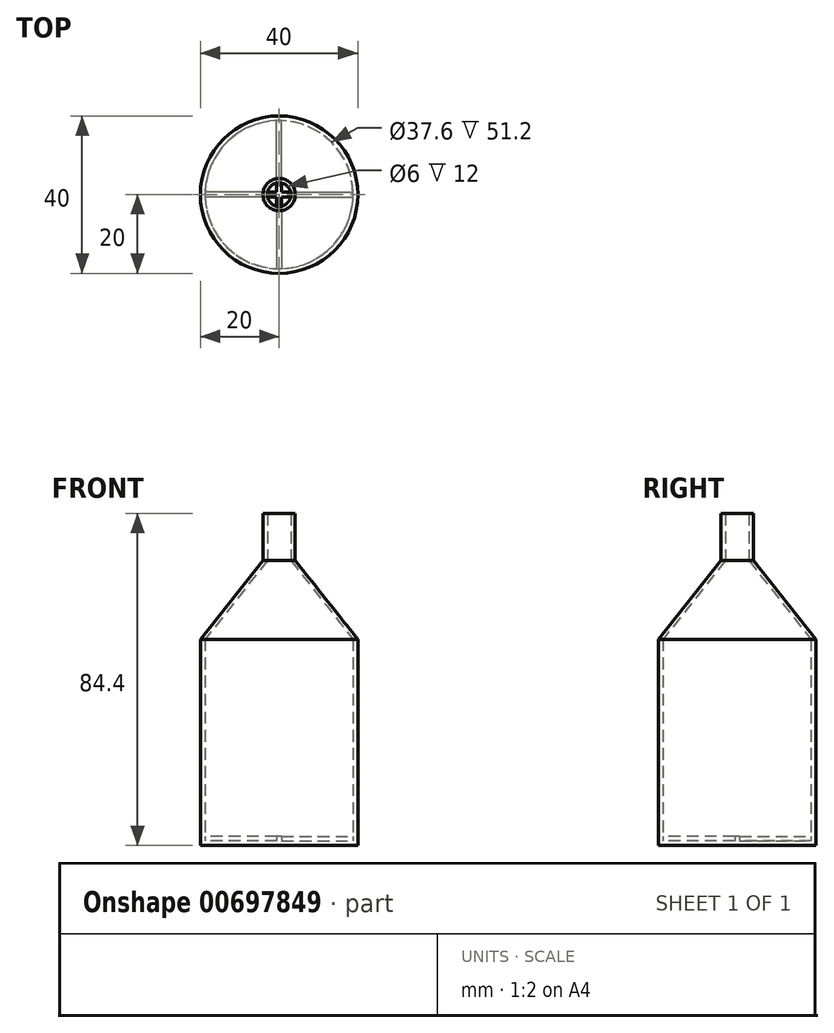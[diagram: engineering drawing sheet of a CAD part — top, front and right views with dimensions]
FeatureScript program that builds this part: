
annotation { "Feature Type Name" : "Feature", "Feature Type Description" : "" }
export const myFeature = defineFeature(function(context is Context, id is Id, definition is map)
    precondition{}
    {
        {
            assignVariable(context, id + "F0", {"name" : "Width", "anyValue" : 0.6});
        }
        {
            var Q0;
            Q0=qCreatedBy(makeId("Top.planeOp"),FACE);
            var sketch = newSketch(context, id + "F1", { "sketchPlane" : qUnion([Q0])});
            skCircle(sketch, "E0", {"center": v(0, 0) * mm, "radius": 20 * mm});
            skLineSegment(sketch, "E1", {"start": v(0, 0) * mm, "end": v(20, 0) * mm, "construction": true});
            skLineSegment(sketch, "E2", {"start": v(0, 0) * mm, "end": v(-20, 0) * mm, "construction": true});
            skLineSegment(sketch, "E3", {"start": v(0, 0) * mm, "end": v(0, 20) * mm, "construction": true});
            skLineSegment(sketch, "E4", {"start": v(0, 0) * mm, "end": v(0, -20) * mm, "construction": true});
            skLineSegment(sketch, "E5.0", {"start": v(0.6, 0.6) * mm, "end": v(0.6, 18.8) * mm});
            skLineSegment(sketch, "E6.0", {"start": v(-0.6, 0.6) * mm, "end": v(-0.6, 18.8) * mm});
            skLineSegment(sketch, "E7.0", {"start": v(-0.6, 0.6) * mm, "end": v(-18.8, 0.6) * mm});
            skLineSegment(sketch, "E8.0", {"start": v(-0.6, -0.6) * mm, "end": v(-18.8, -0.6) * mm});
            skLineSegment(sketch, "E9.0", {"start": v(0.6, -0.6) * mm, "end": v(18.8, -0.6) * mm});
            skLineSegment(sketch, "E10.0", {"start": v(0.6, 0.6) * mm, "end": v(18.8, 0.6) * mm});
            skLineSegment(sketch, "E11.0", {"start": v(-0.6, -0.6) * mm, "end": v(-0.6, -18.8) * mm});
            skLineSegment(sketch, "E12.0", {"start": v(0.6, -0.6) * mm, "end": v(0.6, -18.8) * mm});
            skArc(sketch, "E13.0", {"start": v(-18.8, -0.6) * mm, "mid": v(-13.3, -13.3) * mm, "end": v(-0.6, -18.8) * mm});
            skArc(sketch, "E14.trimOffspring", {"start": v(18.8, 0.6) * mm, "mid": v(13.3, 13.3) * mm, "end": v(0.6, 18.8) * mm});
            skArc(sketch, "E15.trimOffspring", {"start": v(0.6, -18.8) * mm, "mid": v(13.3, -13.3) * mm, "end": v(18.8, -0.6) * mm});
            skArc(sketch, "E16.trimOffspring", {"start": v(-0.6, 18.8) * mm, "mid": v(-13.3, 13.3) * mm, "end": v(-18.8, 0.6) * mm});
            skSolve(sketch);
        }
        {
            var Q0;
            Q0=makeQuery(id+"F1.imprint","IMPRINT",FACE,{"disambiguationData":[TD([[makeQuery(id+"F1.imprint","IMPRINT",EDGE,{"derivedFrom":sQuery(id+"F1.wireOp",EDGE,"E0")}),1.0]])]});
            extrude(context, id + "F2", {"entities" : qUnion([Q0]), "depth" : (getVariable(context, 'Width') * 2) * mm, "offsetDistance" : 25 * mm});
        }
        {
            var Q0;
            Q0=qCreatedBy(makeId("Top.planeOp"),FACE);
            var sketch = newSketch(context, id + "F3", { "sketchPlane" : qUnion([Q0])});
            skCircle(sketch, "E17.0", {"center": v(0, 0) * mm, "radius": 20 * mm});
            skSolve(sketch);
        }
        {
            var Q0;
            Q0=makeQuery(id+"F3.imprint","IMPRINT",FACE,{"disambiguationData":[TD([[makeQuery(id+"F3.imprint","IMPRINT",EDGE,{"derivedFrom":sQuery(id+"F3.wireOp",EDGE,"E17.0")}),1.0]])]});
            extrude(context, id + "F4", {"entities" : qUnion([Q0]), "operationType" : NewBodyOperationType.ADD, "oppositeDirection" : true, "depth" : (getVariable(context, 'Width') * 2) * mm, "offsetDistance" : 25 * mm});
        }
        {
            var Q0;
            Q0=makeQuery(id+"F2.opExtrude","CAP_FACE",FACE,{"disambiguationData":[OSD([sQuery(id+"F1.wireOp",EDGE,"E0"),sQuery(id+"F1.wireOp",EDGE,"E5.0"),sQuery(id+"F1.wireOp",EDGE,"E6.0"),sQuery(id+"F1.wireOp",EDGE,"E7.0"),sQuery(id+"F1.wireOp",EDGE,"E8.0"),sQuery(id+"F1.wireOp",EDGE,"E9.0"),sQuery(id+"F1.wireOp",EDGE,"E10.0"),sQuery(id+"F1.wireOp",EDGE,"E11.0"),sQuery(id+"F1.wireOp",EDGE,"E12.0"),sQuery(id+"F1.wireOp",EDGE,"E13.0"),sQuery(id+"F1.wireOp",EDGE,"E14.trimOffspring"),sQuery(id+"F1.wireOp",EDGE,"E15.trimOffspring"),sQuery(id+"F1.wireOp",EDGE,"E16.trimOffspring")])],"isStart":false});
            cPlane(context, id + "F5", {"entities" : qUnion([Q0]), "cplaneType" : CPlaneType.OFFSET, "offset" : 0 * mm, "width" : 150 * mm, "height" : 150 * mm});
        }
        {
            var Q0;
            Q0=qCreatedBy(id+"F5.planeOp",FACE);
            var sketch = newSketch(context, id + "F6", { "sketchPlane" : qUnion([Q0])});
            skCircle(sketch, "E18.0", {"center": v(0, 0) * mm, "radius": 20 * mm});
            skCircle(sketch, "E19.0", {"center": v(0, 0) * mm, "radius": 18.8 * mm});
            skSolve(sketch);
        }
        {
            var Q0;
            Q0=makeQuery(id+"F6.imprint","IMPRINT",FACE,{"disambiguationData":[TD([[makeQuery(id+"F6.imprint","IMPRINT",EDGE,{"derivedFrom":sQuery(id+"F6.wireOp",EDGE,"E18.0")}),1.0]])]});
            extrude(context, id + "F7", {"entities" : qUnion([Q0]), "operationType" : NewBodyOperationType.ADD, "depth" : 50 * mm, "offsetDistance" : 25 * mm});
        }
        {
            var Q0;
            Q0=makeQuery(id+"F7.opExtrude","CAP_FACE",FACE,{"disambiguationData":[OSD([sQuery(id+"F6.wireOp",EDGE,"E18.0"),sQuery(id+"F6.wireOp",EDGE,"E19.0")])],"isStart":false});
            cPlane(context, id + "F8", {"entities" : qUnion([Q0]), "cplaneType" : CPlaneType.OFFSET, "offset" : 0 * mm, "width" : 150 * mm, "height" : 150 * mm});
        }
        {
            var Q0;
            Q0=qCreatedBy(id+"F8.planeOp",FACE);
            var sketch = newSketch(context, id + "F9", { "sketchPlane" : qUnion([Q0])});
            skCircle(sketch, "E20.0", {"center": v(0, 0) * mm, "radius": 20 * mm});
            skSolve(sketch);
        }
        {
            var Q0;
            Q0=qCreatedBy(id+"F8.planeOp",FACE);
            cPlane(context, id + "F10", {"entities" : qUnion([Q0]), "cplaneType" : CPlaneType.OFFSET, "offset" : 20 * mm, "width" : 150 * mm, "height" : 150 * mm});
        }
        {
            var Q0;
            Q0=qCreatedBy(id+"F10.planeOp",FACE);
            var sketch = newSketch(context, id + "F11", { "sketchPlane" : qUnion([Q0])});
            skCircle(sketch, "E21", {"center": v(0, 0) * mm, "radius": 4.1 * mm});
            skSolve(sketch);
        }
        {
            var Q1;
            Q1=makeQuery(id+"F9.imprint","IMPRINT",FACE,{"disambiguationData":[TD([[makeQuery(id+"F9.imprint","IMPRINT",EDGE,{"derivedFrom":sQuery(id+"F9.wireOp",EDGE,"E20.0")}),1.0]])]});
            var Q2;
            Q2=makeQuery(id+"F11.imprint","IMPRINT",FACE,{"disambiguationData":[TD([[makeQuery(id+"F11.imprint","IMPRINT",EDGE,{"derivedFrom":sQuery(id+"F11.wireOp",EDGE,"E21")}),1.0]])]});
            loft(context, id + "F12", {"operationType" : NewBodyOperationType.ADD, "sheetProfilesArray" : [{ "sheetProfileEntities" : qUnion([Q1]) }, { "sheetProfileEntities" : qUnion([Q2]) }]});
        }
        {
            var Q0;
            Q0=makeQuery(id+"F12.opLoft","CAP_FACE",FACE,{"disambiguationData":[OSD([makeQuery(id+"F11.imprint","IMPRINT",FACE,{"disambiguationData":[TD([[makeQuery(id+"F11.imprint","IMPRINT",EDGE,{"derivedFrom":sQuery(id+"F11.wireOp",EDGE,"E21")}),1.0]])]})])],"isStart":true});
            extrude(context, id + "F13", {"entities" : qUnion([Q0]), "operationType" : NewBodyOperationType.ADD, "depth" : 12 * mm, "offsetDistance" : 25 * mm});
        }
        {
            var Q0;
            Q0=qCreatedBy(id+"F8.planeOp",FACE);
            var sketch = newSketch(context, id + "F14", { "sketchPlane" : qUnion([Q0])});
            skCircle(sketch, "E22.0", {"center": v(0, 0) * mm, "radius": 20 * mm, "construction": true});
            skCircle(sketch, "E23.0", {"center": v(0, 0) * mm, "radius": 18.8 * mm});
            skSolve(sketch);
        }
        {
            var Q0;
            Q0=qCreatedBy(id+"F10.planeOp",FACE);
            var sketch = newSketch(context, id + "F15", { "sketchPlane" : qUnion([Q0])});
            skCircle(sketch, "E24.0", {"center": v(0, 0) * mm, "radius": 4.1 * mm, "construction": true});
            skCircle(sketch, "E25.0", {"center": v(0, 0) * mm, "radius": 3 * mm});
            skSolve(sketch);
        }
        {
            var Q0;
            Q0 = qSketchRegion(id + "F15", true);
            extrude(context, id + "F16", {"entities" : qUnion([Q0]), "operationType" : NewBodyOperationType.REMOVE, "depth" : 25 * mm, "offsetDistance" : 25 * mm});
        }
        {
            var Q1;
            Q1 = qSketchRegion(id + "F14", true);
            var Q2;
            Q2 = qSketchRegion(id + "F15", true);
            loft(context, id + "F17", {"operationType" : NewBodyOperationType.REMOVE, "sheetProfilesArray" : [{ "sheetProfileEntities" : qUnion([Q1]) }, { "sheetProfileEntities" : qUnion([Q2]) }]});
        }
    });
